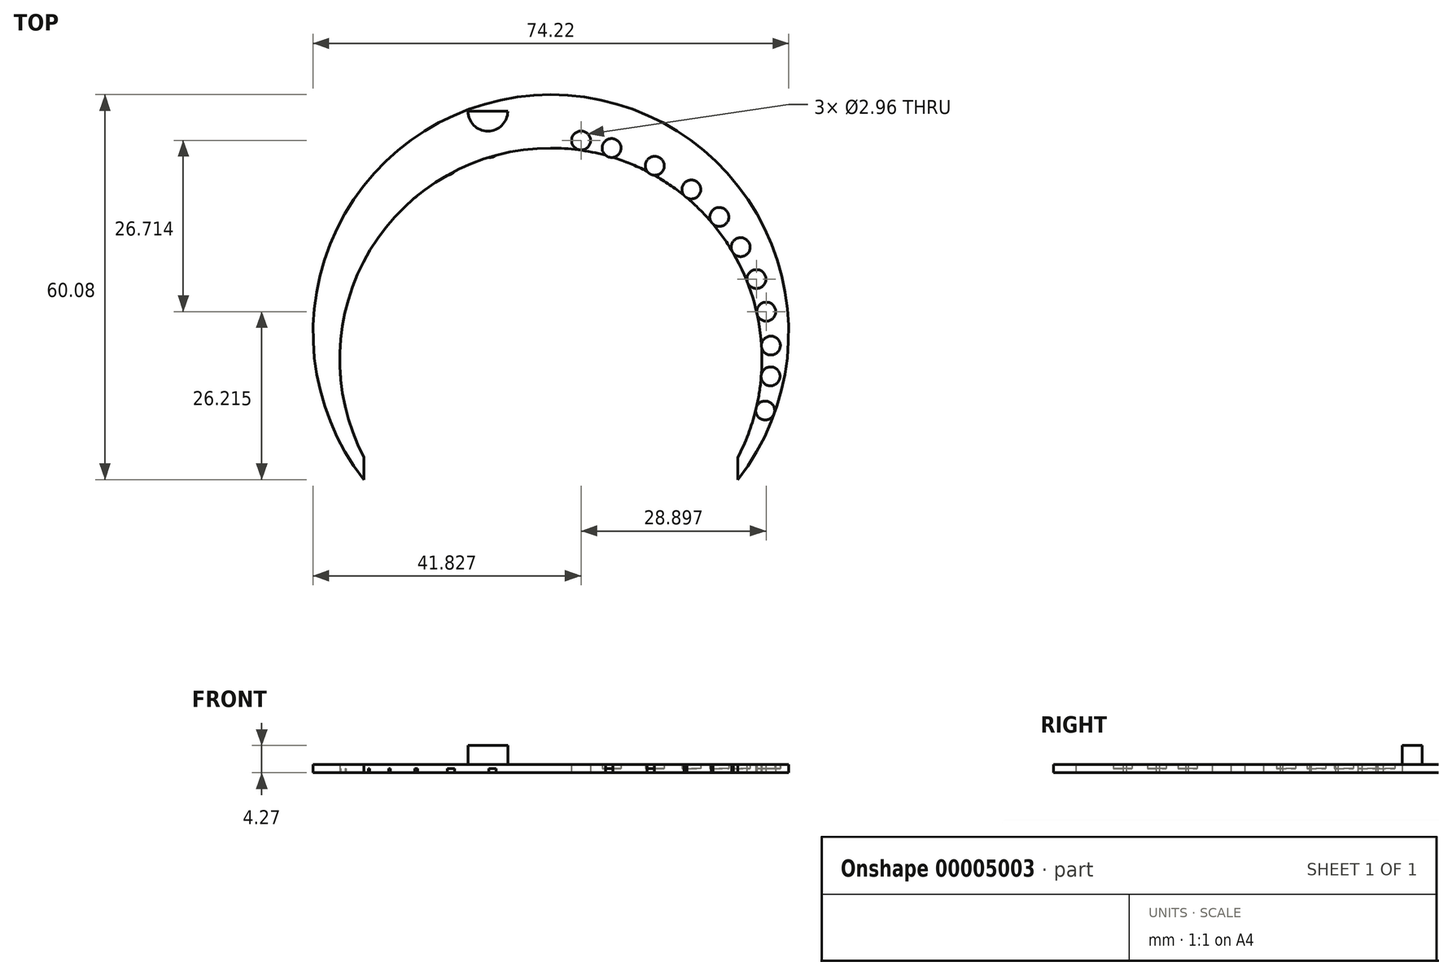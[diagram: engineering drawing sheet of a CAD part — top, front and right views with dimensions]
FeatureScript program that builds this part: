
annotation { "Feature Type Name" : "Feature", "Feature Type Description" : "" }
export const myFeature = defineFeature(function(context is Context, id is Id, definition is map)
    precondition{}
    {
        {
            var Q0;
            Q0=qCreatedBy(makeId("Top.planeOp"),FACE);
            var sketch = newSketch(context, id + "F0", { "sketchPlane" : qUnion([Q0])});
            skArc(sketch, "E0", {"start": v(-0.03, 37.14) * mm, "mid": v(-33.4, 16.22) * mm, "end": v(-29.2, -22.94) * mm});
            skArc(sketch, "E1", {"start": v(0.03, 28.81) * mm, "mid": v(-28.2, 12.92) * mm, "end": v(-29.2, -19.47) * mm});
            skLineSegment(sketch, "E2", {"start": v(-29.2, -19.47) * mm, "end": v(-29.2, -22.94) * mm});
            skCircle(sketch, "E3", {"center": v(-33.49, -12.16) * mm, "radius": 1.48 * mm});
            skCircle(sketch, "E4", {"center": v(-33.64, 3.28) * mm, "radius": 1.48 * mm});
            skPoint(sketch, "E5.startSnap0", {"position": v(0.03, 28.81) * mm});
            skCircle(sketch, "E6", {"center": v(-34.33, -6.83) * mm, "radius": 1.48 * mm});
            skCircle(sketch, "E7", {"center": v(-34.38, -2.02) * mm, "radius": 1.48 * mm});
            skCircle(sketch, "E8", {"center": v(-32.11, 8.36) * mm, "radius": 1.48 * mm});
            skCircle(sketch, "E9", {"center": v(-29.66, 13.34) * mm, "radius": 1.48 * mm});
            skCircle(sketch, "E10", {"center": v(-26.32, 18.06) * mm, "radius": 1.48 * mm});
            skCircle(sketch, "E11", {"center": v(-21.96, 22.35) * mm, "radius": 1.48 * mm});
            skCircle(sketch, "E12", {"center": v(-16.26, 26.04) * mm, "radius": 1.48 * mm});
            skCircle(sketch, "E13", {"center": v(-9.52, 28.81) * mm, "radius": 1.48 * mm});
            skArc(sketch, "E14", {"start": v(-0.03, 31.95) * mm, "mid": v(-1.46, 30.48) * mm, "end": v(-0.03, 29) * mm});
            skCircle(sketch, "E15", {"center": v(-4.75, 29.99) * mm, "radius": 1.48 * mm});
            skLineSegment(sketch, "E16.MirrorCS", {"start": v(29.15, -19.47) * mm, "end": v(29.15, -22.94) * mm});
            skArc(sketch, "E17.MirrorCS", {"start": v(-0.03, 31.95) * mm, "mid": v(1.4, 30.48) * mm, "end": v(-0.03, 29) * mm});
            skCircle(sketch, "E18.MirrorC", {"center": v(16.2, 26.04) * mm, "radius": 1.48 * mm});
            skCircle(sketch, "E19.MirrorC", {"center": v(21.9, 22.35) * mm, "radius": 1.48 * mm});
            skCircle(sketch, "E20.MirrorC", {"center": v(26.26, 18.06) * mm, "radius": 1.48 * mm});
            skCircle(sketch, "E21.MirrorC", {"center": v(29.6, 13.34) * mm, "radius": 1.48 * mm});
            skCircle(sketch, "E22.MirrorC", {"center": v(32.05, 8.36) * mm, "radius": 1.48 * mm});
            skCircle(sketch, "E23.MirrorC", {"center": v(33.58, 3.28) * mm, "radius": 1.48 * mm});
            skCircle(sketch, "E24.MirrorC", {"center": v(34.32, -2.02) * mm, "radius": 1.48 * mm});
            skCircle(sketch, "E25.MirrorC", {"center": v(9.46, 28.81) * mm, "radius": 1.48 * mm});
            skPoint(sketch, "E26.MirrorP", {"position": v(-0.09, 28.81) * mm});
            skCircle(sketch, "E27.MirrorC", {"center": v(34.27, -6.83) * mm, "radius": 1.48 * mm});
            skArc(sketch, "E28.MirrorCS", {"start": v(-0.09, 28.81) * mm, "mid": v(28.15, 12.92) * mm, "end": v(29.15, -19.47) * mm});
            skCircle(sketch, "E29.MirrorC", {"center": v(33.43, -12.16) * mm, "radius": 1.48 * mm});
            skArc(sketch, "E30.MirrorCS", {"start": v(-0.03, 37.14) * mm, "mid": v(33.35, 16.22) * mm, "end": v(29.15, -22.94) * mm});
            skCircle(sketch, "E31.MirrorC", {"center": v(4.69, 29.99) * mm, "radius": 1.48 * mm});
            skPoint(sketch, "E5.start.orphan", {"position": v(-0.03, 28.81) * mm});
            skSolve(sketch);
        }
        {
            var Q0;
            Q0=makeQuery(id+"F0.imprint","IMPRINT",FACE,{"disambiguationData":[TD([[makeQuery(id+"F0.imprint","IMPRINT",EDGE,{"derivedFrom":sQuery(id+"F0.wireOp",EDGE,"E4")}),1.0]])]});
            var Q1;
            Q1=makeQuery(id+"F0.imprint","IMPRINT",FACE,{"disambiguationData":[TD([[makeQuery(id+"F0.imprint","IMPRINT",EDGE,{"derivedFrom":sQuery(id+"F0.wireOp",EDGE,"E22.MirrorC")}),-1.0]])]});
            var Q2;
            {var subQ0=sQuery(id+"F0.wireOp",EDGE,"E7");var subQ1=sQuery(id+"F0.wireOp",EDGE,"E1");var subQ2=makeQuery(id+"F0.imprint","INTERSECT",VERTEX,{"disambiguationData":[OD(0.0)],"derivedFrom":[subQ1,subQ0]});Q2=makeQuery(id+"F0.imprint","IMPRINT",FACE,{"disambiguationData":[TD([[makeQuery(id+"F0.imprint","IMPRINT",EDGE,{"disambiguationData":[TD([[subQ2,-1.0]])],"derivedFrom":subQ1}),-1.0]])]});}
            var Q3;
            {var subQ0=sQuery(id+"F0.wireOp",EDGE,"E6");var subQ1=sQuery(id+"F0.wireOp",EDGE,"E1");var subQ2=makeQuery(id+"F0.imprint","INTERSECT",VERTEX,{"disambiguationData":[OD(0.0)],"derivedFrom":[subQ1,subQ0]});Q3=makeQuery(id+"F0.imprint","IMPRINT",FACE,{"disambiguationData":[TD([[makeQuery(id+"F0.imprint","IMPRINT",EDGE,{"disambiguationData":[TD([[subQ2,-1.0]])],"derivedFrom":subQ1}),-1.0]])]});}
            var Q4;
            {var subQ0=sQuery(id+"F0.wireOp",EDGE,"E3");var subQ1=sQuery(id+"F0.wireOp",EDGE,"E1");var subQ2=makeQuery(id+"F0.imprint","INTERSECT",VERTEX,{"disambiguationData":[OD(0.0)],"derivedFrom":[subQ1,subQ0]});Q4=makeQuery(id+"F0.imprint","IMPRINT",FACE,{"disambiguationData":[TD([[makeQuery(id+"F0.imprint","IMPRINT",EDGE,{"disambiguationData":[TD([[subQ2,-1.0]])],"derivedFrom":subQ1}),-1.0]])]});}
            var Q5;
            Q5=makeQuery(id+"F0.imprint","IMPRINT",FACE,{"disambiguationData":[TD([[makeQuery(id+"F0.imprint","IMPRINT",EDGE,{"derivedFrom":sQuery(id+"F0.wireOp",EDGE,"E8")}),1.0]])]});
            var Q6;
            {var subQ0=sQuery(id+"F0.wireOp",EDGE,"E9");var subQ1=sQuery(id+"F0.wireOp",EDGE,"E1");var subQ2=makeQuery(id+"F0.imprint","INTERSECT",VERTEX,{"disambiguationData":[OD(0.0)],"derivedFrom":[subQ1,subQ0]});Q6=makeQuery(id+"F0.imprint","IMPRINT",FACE,{"disambiguationData":[TD([[makeQuery(id+"F0.imprint","IMPRINT",EDGE,{"disambiguationData":[TD([[subQ2,-1.0]])],"derivedFrom":subQ1}),-1.0]])]});}
            var Q7;
            {var subQ0=sQuery(id+"F0.wireOp",EDGE,"E10");var subQ1=sQuery(id+"F0.wireOp",EDGE,"E1");var subQ2=makeQuery(id+"F0.imprint","INTERSECT",VERTEX,{"disambiguationData":[OD(0.0)],"derivedFrom":[subQ1,subQ0]});Q7=makeQuery(id+"F0.imprint","IMPRINT",FACE,{"disambiguationData":[TD([[makeQuery(id+"F0.imprint","IMPRINT",EDGE,{"disambiguationData":[TD([[subQ2,-1.0]])],"derivedFrom":subQ1}),-1.0]])]});}
            var Q8;
            {var subQ0=sQuery(id+"F0.wireOp",EDGE,"E11");var subQ1=sQuery(id+"F0.wireOp",EDGE,"E1");var subQ2=makeQuery(id+"F0.imprint","INTERSECT",VERTEX,{"disambiguationData":[OD(0.0)],"derivedFrom":[subQ1,subQ0]});Q8=makeQuery(id+"F0.imprint","IMPRINT",FACE,{"disambiguationData":[TD([[makeQuery(id+"F0.imprint","IMPRINT",EDGE,{"disambiguationData":[TD([[subQ2,-1.0]])],"derivedFrom":subQ1}),-1.0]])]});}
            var Q9;
            {var subQ0=sQuery(id+"F0.wireOp",EDGE,"E12");var subQ1=sQuery(id+"F0.wireOp",EDGE,"E1");var subQ2=makeQuery(id+"F0.imprint","INTERSECT",VERTEX,{"disambiguationData":[OD(0.0)],"derivedFrom":[subQ1,subQ0]});Q9=makeQuery(id+"F0.imprint","IMPRINT",FACE,{"disambiguationData":[TD([[makeQuery(id+"F0.imprint","IMPRINT",EDGE,{"disambiguationData":[TD([[subQ2,-1.0]])],"derivedFrom":subQ1}),-1.0]])]});}
            var Q10;
            {var subQ0=sQuery(id+"F0.wireOp",EDGE,"E13");var subQ1=sQuery(id+"F0.wireOp",EDGE,"E1");var subQ2=makeQuery(id+"F0.imprint","INTERSECT",VERTEX,{"disambiguationData":[OD(0.0)],"derivedFrom":[subQ1,subQ0]});Q10=makeQuery(id+"F0.imprint","IMPRINT",FACE,{"disambiguationData":[TD([[makeQuery(id+"F0.imprint","IMPRINT",EDGE,{"disambiguationData":[TD([[subQ2,-1.0]])],"derivedFrom":subQ1}),-1.0]])]});}
            var Q11;
            Q11=makeQuery(id+"F0.imprint","IMPRINT",FACE,{"disambiguationData":[TD([[makeQuery(id+"F0.imprint","IMPRINT",EDGE,{"derivedFrom":sQuery(id+"F0.wireOp",EDGE,"E15")}),1.0]])]});
            var Q12;
            Q12=makeQuery(id+"F0.imprint","IMPRINT",FACE,{"disambiguationData":[TD([[makeQuery(id+"F0.imprint","IMPRINT",EDGE,{"derivedFrom":sQuery(id+"F0.wireOp",EDGE,"E14")}),1.0]])]});
            var Q13;
            {var subQ0=sQuery(id+"F0.wireOp",EDGE,"E28.MirrorCS");var subQ1=sQuery(id+"F0.wireOp",EDGE,"E25.MirrorC");var subQ2=makeQuery(id+"F0.imprint","INTERSECT",VERTEX,{"disambiguationData":[OD(0.0)],"derivedFrom":[subQ1,subQ0]});Q13=makeQuery(id+"F0.imprint","IMPRINT",FACE,{"disambiguationData":[TD([[makeQuery(id+"F0.imprint","IMPRINT",EDGE,{"disambiguationData":[TD([[subQ2,-1.0]])],"derivedFrom":subQ1}),-1.0]])]});}
            var Q14;
            Q14=makeQuery(id+"F0.imprint","IMPRINT",FACE,{"disambiguationData":[TD([[makeQuery(id+"F0.imprint","IMPRINT",EDGE,{"derivedFrom":sQuery(id+"F0.wireOp",EDGE,"E31.MirrorC")}),-1.0]])]});
            var Q15;
            {var subQ0=sQuery(id+"F0.wireOp",EDGE,"E28.MirrorCS");var subQ1=sQuery(id+"F0.wireOp",EDGE,"E18.MirrorC");var subQ2=makeQuery(id+"F0.imprint","INTERSECT",VERTEX,{"disambiguationData":[OD(0.0)],"derivedFrom":[subQ1,subQ0]});Q15=makeQuery(id+"F0.imprint","IMPRINT",FACE,{"disambiguationData":[TD([[makeQuery(id+"F0.imprint","IMPRINT",EDGE,{"disambiguationData":[TD([[subQ2,-1.0]])],"derivedFrom":subQ1}),-1.0]])]});}
            var Q16;
            {var subQ0=sQuery(id+"F0.wireOp",EDGE,"E28.MirrorCS");var subQ1=sQuery(id+"F0.wireOp",EDGE,"E19.MirrorC");var subQ2=makeQuery(id+"F0.imprint","INTERSECT",VERTEX,{"disambiguationData":[OD(0.0)],"derivedFrom":[subQ1,subQ0]});Q16=makeQuery(id+"F0.imprint","IMPRINT",FACE,{"disambiguationData":[TD([[makeQuery(id+"F0.imprint","IMPRINT",EDGE,{"disambiguationData":[TD([[subQ2,-1.0]])],"derivedFrom":subQ1}),-1.0]])]});}
            var Q17;
            {var subQ0=sQuery(id+"F0.wireOp",EDGE,"E28.MirrorCS");var subQ1=sQuery(id+"F0.wireOp",EDGE,"E20.MirrorC");var subQ2=makeQuery(id+"F0.imprint","INTERSECT",VERTEX,{"disambiguationData":[OD(0.0)],"derivedFrom":[subQ1,subQ0]});Q17=makeQuery(id+"F0.imprint","IMPRINT",FACE,{"disambiguationData":[TD([[makeQuery(id+"F0.imprint","IMPRINT",EDGE,{"disambiguationData":[TD([[subQ2,-1.0]])],"derivedFrom":subQ1}),-1.0]])]});}
            var Q18;
            {var subQ0=sQuery(id+"F0.wireOp",EDGE,"E28.MirrorCS");var subQ1=sQuery(id+"F0.wireOp",EDGE,"E21.MirrorC");var subQ2=makeQuery(id+"F0.imprint","INTERSECT",VERTEX,{"disambiguationData":[OD(0.0)],"derivedFrom":[subQ1,subQ0]});Q18=makeQuery(id+"F0.imprint","IMPRINT",FACE,{"disambiguationData":[TD([[makeQuery(id+"F0.imprint","IMPRINT",EDGE,{"disambiguationData":[TD([[subQ2,-1.0]])],"derivedFrom":subQ1}),-1.0]])]});}
            var Q19;
            Q19=makeQuery(id+"F0.imprint","IMPRINT",FACE,{"disambiguationData":[TD([[makeQuery(id+"F0.imprint","IMPRINT",EDGE,{"derivedFrom":sQuery(id+"F0.wireOp",EDGE,"E23.MirrorC")}),-1.0]])]});
            var Q20;
            {var subQ0=sQuery(id+"F0.wireOp",EDGE,"E28.MirrorCS");var subQ1=sQuery(id+"F0.wireOp",EDGE,"E24.MirrorC");var subQ2=makeQuery(id+"F0.imprint","INTERSECT",VERTEX,{"disambiguationData":[OD(0.0)],"derivedFrom":[subQ1,subQ0]});Q20=makeQuery(id+"F0.imprint","IMPRINT",FACE,{"disambiguationData":[TD([[makeQuery(id+"F0.imprint","IMPRINT",EDGE,{"disambiguationData":[TD([[subQ2,-1.0]])],"derivedFrom":subQ1}),-1.0]])]});}
            var Q21;
            {var subQ0=sQuery(id+"F0.wireOp",EDGE,"E28.MirrorCS");var subQ1=sQuery(id+"F0.wireOp",EDGE,"E27.MirrorC");var subQ2=makeQuery(id+"F0.imprint","INTERSECT",VERTEX,{"disambiguationData":[OD(0.0)],"derivedFrom":[subQ1,subQ0]});Q21=makeQuery(id+"F0.imprint","IMPRINT",FACE,{"disambiguationData":[TD([[makeQuery(id+"F0.imprint","IMPRINT",EDGE,{"disambiguationData":[TD([[subQ2,-1.0]])],"derivedFrom":subQ1}),-1.0]])]});}
            var Q22;
            {var subQ0=sQuery(id+"F0.wireOp",EDGE,"E29.MirrorC");var subQ1=sQuery(id+"F0.wireOp",EDGE,"E28.MirrorCS");var subQ2=makeQuery(id+"F0.imprint","INTERSECT",VERTEX,{"disambiguationData":[OD(0.0)],"derivedFrom":[subQ1,subQ0]});Q22=makeQuery(id+"F0.imprint","IMPRINT",FACE,{"disambiguationData":[TD([[makeQuery(id+"F0.imprint","IMPRINT",EDGE,{"disambiguationData":[TD([[subQ2,-1.0]])],"derivedFrom":subQ1}),1.0]])]});}
            extrude(context, id + "F1", {"entities" : qUnion([Q0, Q1, Q2, Q3, Q4, Q5, Q6, Q7, Q8, Q9, Q10, Q11, Q12, Q13, Q14, Q15, Q16, Q17, Q18, Q19, Q20, Q21, Q22]), "depth" : 1.27 * mm});
        }
        {
            var Q0;
            Q0 = qSketchRegion(id + "F0", true);
            extrude(context, id + "F2", {"entities" : qUnion([Q0]), "depth" : 0.64 * mm});
        }
        {
            var Q0;
            Q0=makeQuery(id+"F2.opExtrude","CAP_FACE",FACE,{"disambiguationData":[OSD([sQuery(id+"F0.wireOp",EDGE,"E0"),sQuery(id+"F0.wireOp",EDGE,"E1"),sQuery(id+"F0.wireOp",EDGE,"E2"),sQuery(id+"F0.wireOp",EDGE,"E3"),sQuery(id+"F0.wireOp",EDGE,"E4"),sQuery(id+"F0.wireOp",EDGE,"E6"),sQuery(id+"F0.wireOp",EDGE,"E7"),sQuery(id+"F0.wireOp",EDGE,"E8"),sQuery(id+"F0.wireOp",EDGE,"E9"),sQuery(id+"F0.wireOp",EDGE,"E10"),sQuery(id+"F0.wireOp",EDGE,"E11"),sQuery(id+"F0.wireOp",EDGE,"E12"),sQuery(id+"F0.wireOp",EDGE,"E13"),sQuery(id+"F0.wireOp",EDGE,"E14"),sQuery(id+"F0.wireOp",EDGE,"E15"),sQuery(id+"F0.wireOp",EDGE,"E16.MirrorCS"),sQuery(id+"F0.wireOp",EDGE,"E17.MirrorCS"),sQuery(id+"F0.wireOp",EDGE,"E18.MirrorC"),sQuery(id+"F0.wireOp",EDGE,"E19.MirrorC"),sQuery(id+"F0.wireOp",EDGE,"E20.MirrorC"),sQuery(id+"F0.wireOp",EDGE,"E21.MirrorC"),sQuery(id+"F0.wireOp",EDGE,"E22.MirrorC"),sQuery(id+"F0.wireOp",EDGE,"E23.MirrorC"),sQuery(id+"F0.wireOp",EDGE,"E24.MirrorC"),sQuery(id+"F0.wireOp",EDGE,"E25.MirrorC"),sQuery(id+"F0.wireOp",EDGE,"E27.MirrorC"),sQuery(id+"F0.wireOp",EDGE,"E28.MirrorCS"),sQuery(id+"F0.wireOp",EDGE,"E29.MirrorC"),sQuery(id+"F0.wireOp",EDGE,"E30.MirrorCS"),sQuery(id+"F0.wireOp",EDGE,"E31.MirrorC")])],"isStart":false});
            var sketch = newSketch(context, id + "F3", { "sketchPlane" : qUnion([Q0])});
            skLineSegment(sketch, "E32.bottom", {"start": v(-13.58, 34.57) * mm, "end": v(-6.14, 34.57) * mm});
            skLineSegment(sketch, "E32.top", {"start": v(-13.58, 31.46) * mm, "end": v(-6.14, 31.46) * mm});
            skLineSegment(sketch, "E32.left", {"start": v(-13.58, 34.57) * mm, "end": v(-13.58, 31.46) * mm});
            skLineSegment(sketch, "E32.right", {"start": v(-6.14, 34.57) * mm, "end": v(-6.14, 31.46) * mm});
            skCircle(sketch, "E33", {"center": v(-9.86, 34.57) * mm, "radius": 3.1 * mm});
            skSolve(sketch);
        }
        {
            var Q0;
            {var subQ0=sQuery(id+"F3.wireOp",EDGE,"E33");var subQ1=sQuery(id+"F3.wireOp",EDGE,"E32.bottom");var subQ2=makeQuery(id+"F3.imprint","INTERSECT",VERTEX,{"disambiguationData":[OD(0.0)],"derivedFrom":[subQ1,subQ0]});Q0=makeQuery(id+"F3.imprint","IMPRINT",FACE,{"disambiguationData":[TD([[makeQuery(id+"F3.imprint","IMPRINT",EDGE,{"disambiguationData":[TD([[subQ2,-1.0]])],"derivedFrom":subQ1}),-1.0]])]});}
            extrude(context, id + "F4", {"entities" : qUnion([Q0]), "operationType" : NewBodyOperationType.ADD, "depth" : 3.63 * mm});
        }
    });
